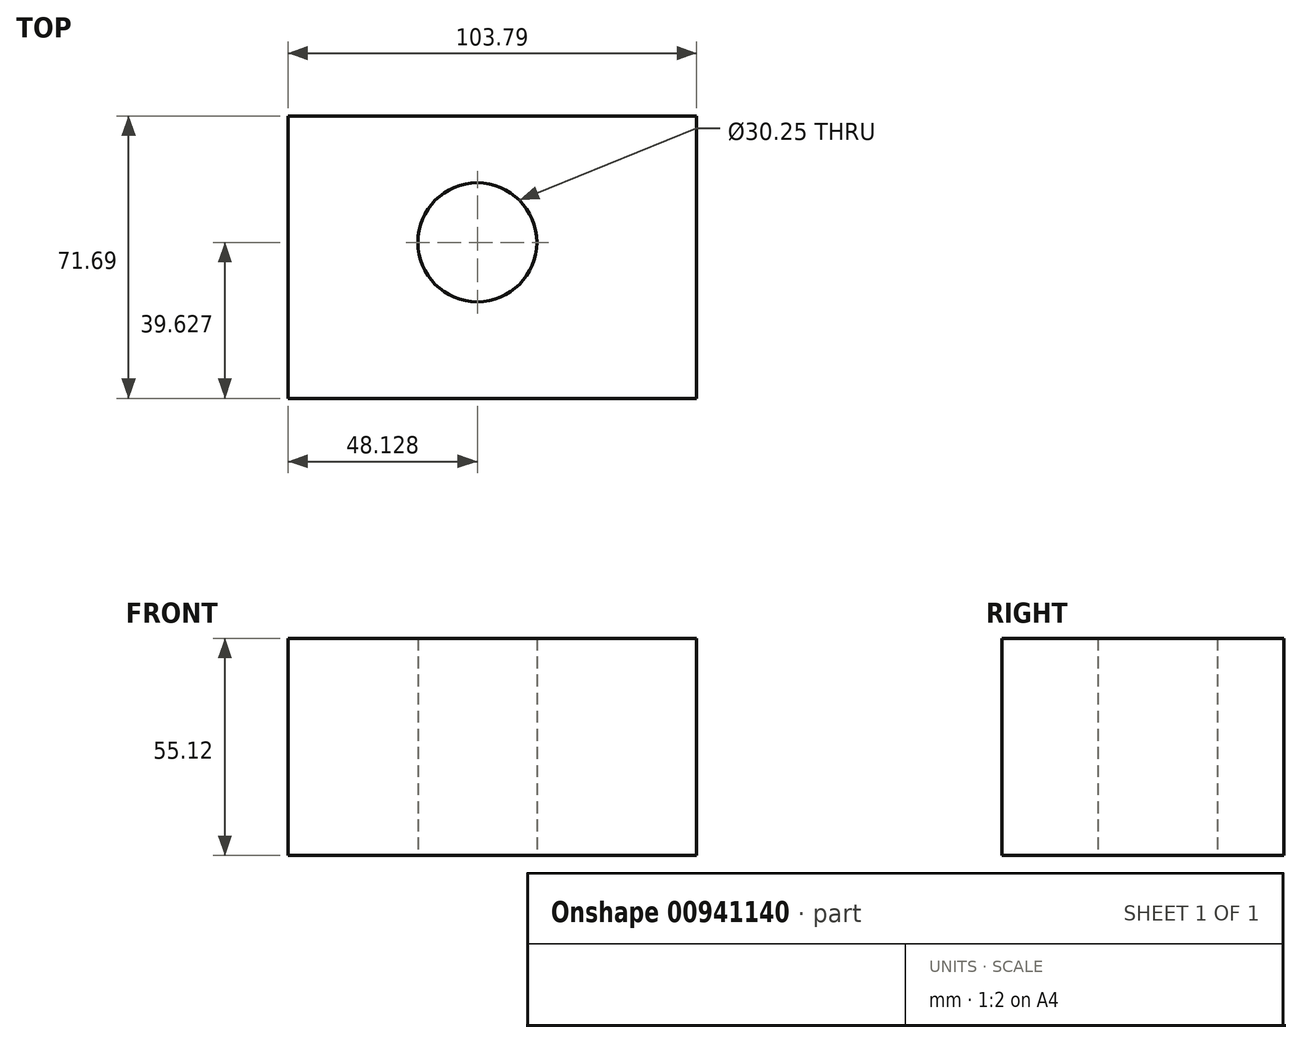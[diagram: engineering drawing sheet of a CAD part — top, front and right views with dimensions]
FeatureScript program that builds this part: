
annotation { "Feature Type Name" : "Feature", "Feature Type Description" : "" }
export const myFeature = defineFeature(function(context is Context, id is Id, definition is map)
    precondition{}
    {
        {
            var Q0;
            Q0=qCreatedBy(makeId("Top.planeOp"),FACE);
            var sketch = newSketch(context, id + "F0", { "sketchPlane" : qUnion([Q0])});
            skLineSegment(sketch, "E0.bottom", {"start": v(0, 0) * mm, "end": v(103.79, 0) * mm});
            skLineSegment(sketch, "E0.top", {"start": v(0, 71.7) * mm, "end": v(103.79, 71.7) * mm});
            skLineSegment(sketch, "E0.left", {"start": v(0, 0) * mm, "end": v(0, 71.7) * mm});
            skLineSegment(sketch, "E0.right", {"start": v(103.79, 0) * mm, "end": v(103.79, 71.7) * mm});
            skCircle(sketch, "E1", {"center": v(48.13, 39.63) * mm, "radius": 15.12 * mm});
            skSolve(sketch);
        }
        {
            var Q0;
            Q0=makeQuery(id+"F0.imprint","IMPRINT",FACE,{"disambiguationData":[TD([[makeQuery(id+"F0.imprint","IMPRINT",EDGE,{"derivedFrom":sQuery(id+"F0.wireOp",EDGE,"E0.bottom")}),1.0]])]});
            extrude(context, id + "F1", {"entities" : qUnion([Q0]), "depth" : 55.12 * mm, "offsetDistance" : 25.4 * mm});
        }
    });
